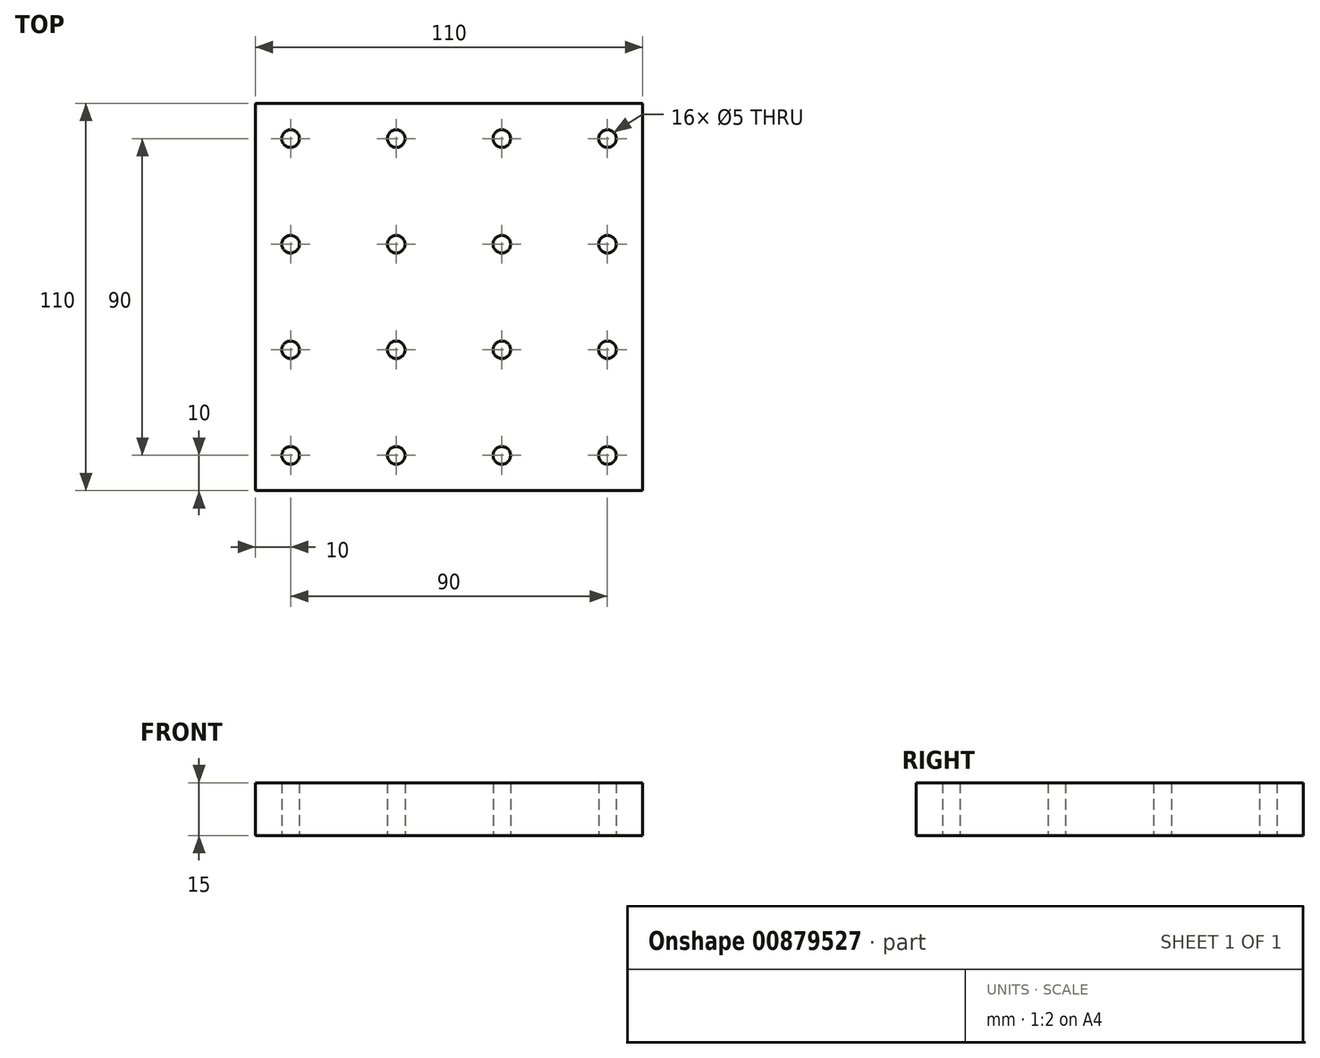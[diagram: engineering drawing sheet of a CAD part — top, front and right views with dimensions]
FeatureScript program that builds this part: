
annotation { "Feature Type Name" : "Feature", "Feature Type Description" : "" }
export const myFeature = defineFeature(function(context is Context, id is Id, definition is map)
    precondition{}
    {
        {
            var Q0;
            Q0=qCreatedBy(makeId("Top.planeOp"),FACE);
            var sketch = newSketch(context, id + "F0", { "sketchPlane" : qUnion([Q0])});
            skLineSegment(sketch, "E0.bottom", {"start": v(55, -55) * mm, "end": v(-55, -55) * mm});
            skLineSegment(sketch, "E0.top", {"start": v(55, 55) * mm, "end": v(-55, 55) * mm});
            skLineSegment(sketch, "E0.left", {"start": v(55, -55) * mm, "end": v(55, 55) * mm});
            skLineSegment(sketch, "E0.right", {"start": v(-55, -55) * mm, "end": v(-55, 55) * mm});
            skCircle(sketch, "E1", {"center": v(-15, -45) * mm, "radius": 2.5 * mm});
            skCircle(sketch, "E2", {"center": v(15, -45) * mm, "radius": 2.5 * mm});
            skCircle(sketch, "E3", {"center": v(45, -45) * mm, "radius": 2.5 * mm});
            skCircle(sketch, "E4", {"center": v(45, -15) * mm, "radius": 2.5 * mm});
            skCircle(sketch, "E5", {"center": v(15, -15) * mm, "radius": 2.5 * mm});
            skCircle(sketch, "E6", {"center": v(-15, -15) * mm, "radius": 2.5 * mm});
            skCircle(sketch, "E7", {"center": v(-45, -15) * mm, "radius": 2.5 * mm});
            skCircle(sketch, "E8", {"center": v(-45, 15) * mm, "radius": 2.5 * mm});
            skCircle(sketch, "E9", {"center": v(-15, 15) * mm, "radius": 2.5 * mm});
            skCircle(sketch, "E10", {"center": v(15, 15) * mm, "radius": 2.5 * mm});
            skCircle(sketch, "E11", {"center": v(45, 15) * mm, "radius": 2.5 * mm});
            skCircle(sketch, "E12", {"center": v(45, 45) * mm, "radius": 2.5 * mm});
            skCircle(sketch, "E13", {"center": v(15, 45) * mm, "radius": 2.5 * mm});
            skCircle(sketch, "E14", {"center": v(-15, 45) * mm, "radius": 2.5 * mm});
            skCircle(sketch, "E15", {"center": v(-45, 45) * mm, "radius": 2.5 * mm});
            skCircle(sketch, "E16", {"center": v(-45, -45) * mm, "radius": 2.5 * mm});
            skSolve(sketch);
        }
        {
            var Q0;
            Q0 = qSketchRegion(id + "F0", true);
            extrude(context, id + "F1", {"entities" : qUnion([Q0]), "depth" : 15 * mm, "offsetDistance" : 25 * mm});
        }
        {
            var Q0;
            Q0=sQuery(id+"F0.wireOp",EDGE,"E1");
            var Q1;
            Q1=sQuery(id+"F0.wireOp",EDGE,"E6");
            var Q2;
            Q2=sQuery(id+"F0.wireOp",EDGE,"E9");
            var Q3;
            Q3=sQuery(id+"F0.wireOp",EDGE,"E14");
            var Q4;
            Q4=sQuery(id+"F0.wireOp",EDGE,"E15");
            var Q5;
            Q5=sQuery(id+"F0.wireOp",EDGE,"E8");
            var Q6;
            Q6=sQuery(id+"F0.wireOp",EDGE,"E7");
            var Q7;
            Q7=sQuery(id+"F0.wireOp",EDGE,"E16");
            var Q8;
            Q8=sQuery(id+"F0.wireOp",EDGE,"E2");
            var Q9;
            Q9=sQuery(id+"F0.wireOp",EDGE,"E3");
            var Q10;
            Q10=sQuery(id+"F0.wireOp",EDGE,"E4");
            var Q11;
            Q11=sQuery(id+"F0.wireOp",EDGE,"E5");
            var Q12;
            Q12=sQuery(id+"F0.wireOp",EDGE,"E10");
            var Q13;
            Q13=sQuery(id+"F0.wireOp",EDGE,"E11");
            var Q14;
            Q14=sQuery(id+"F0.wireOp",EDGE,"E12");
            var Q15;
            Q15=sQuery(id+"F0.wireOp",EDGE,"E13");
            extrude(context, id + "F2", {"bodyType" : ToolBodyType.SURFACE, "surfaceEntities" : qUnion([Q0, Q1, Q2, Q3, Q4, Q5, Q6, Q7, Q8, Q9, Q10, Q11, Q12, Q13, Q14, Q15]), "depth" : 75 * mm, "offsetDistance" : 25 * mm});
        }
    });
